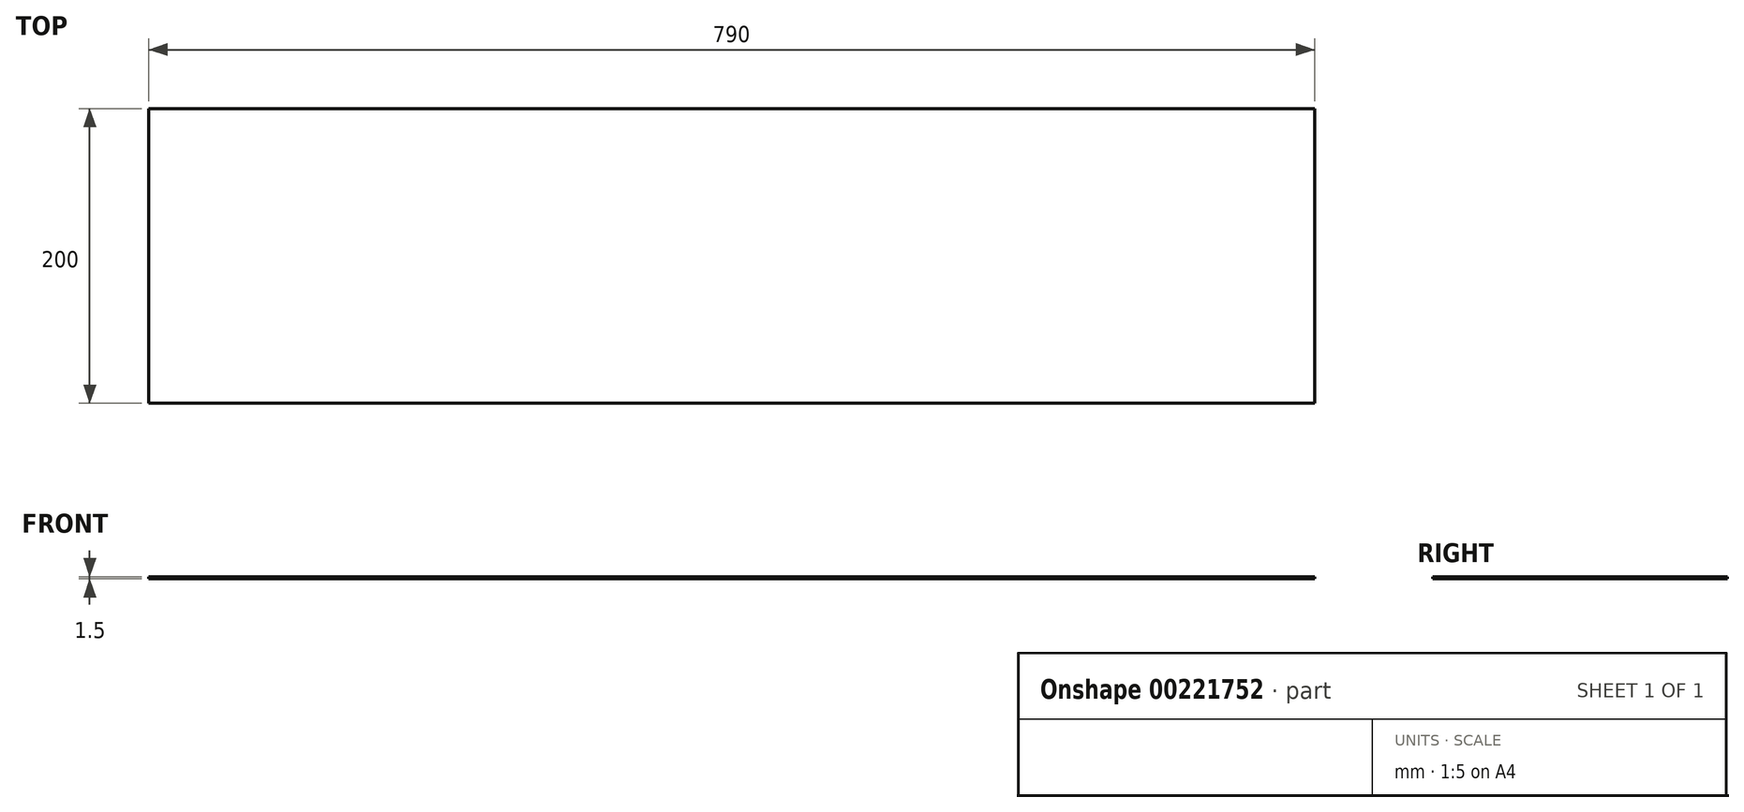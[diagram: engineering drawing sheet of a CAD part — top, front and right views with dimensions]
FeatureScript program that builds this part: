
annotation { "Feature Type Name" : "Feature", "Feature Type Description" : "" }
export const myFeature = defineFeature(function(context is Context, id is Id, definition is map)
    precondition{}
    {
        {
            var Q0;
            Q0=qCreatedBy(makeId("Top.planeOp"),FACE);
            var sketch = newSketch(context, id + "F0", { "sketchPlane" : qUnion([Q0])});
            skLineSegment(sketch, "E0.bottom", {"start": v(-395, 100) * mm, "end": v(395, 100) * mm});
            skLineSegment(sketch, "E0.top", {"start": v(-395, -100) * mm, "end": v(395, -100) * mm});
            skLineSegment(sketch, "E0.left", {"start": v(-395, 100) * mm, "end": v(-395, -100) * mm});
            skLineSegment(sketch, "E0.right", {"start": v(395, 100) * mm, "end": v(395, -100) * mm});
            skPoint(sketch, "E0.middle", {"position": v(0, 0) * mm});
            skSolve(sketch);
        }
        {
            var Q0;
            Q0 = qSketchRegion(id + "F0", true);
            extrude(context, id + "F1", {"entities" : qUnion([Q0]), "depth" : 1.5 * mm});
        }
    });
